# Revit family: PDU medido 0U
name_source: partatom
category: Installations électriques
units: mm (PartAtom-declared; Revit-internal decimal feet)

## family parameters
Basée sur le plan de construction = Non
Conserver l'orientation des annotations = Non
Cote de connecteur circulaire = Utiliser le diamètre
Couper avec des vides une fois chargée = Non
Numéro OmniClass = 23.80.00.00
Partagée = Non
Point de calcul de pièce = Non
Titre OmniClass = Electric Power and Lighting
Toujours verticalement = Oui
Type d'élément = Normal

## types (16) — shared parameters
Clase de aplicación = EC002762
Color = Negro
Conectable con internet box = Oui
Consumo pasivo = 0 mA
Dirección de montaje = Vertical
E-catalogo enlace = https://www.legrand.fr
Fabricant = LEGRAND
Formulación BIM = Linkeo DATA CENTER BASIC PDU
Frecuencia eléctrica = 50-50
Función = Unidad DE DISTRIBUTION D'ENERGIE
IP = IP40
Marcaje = Non
Numero RAL = 9017
Prise_alimentation = Alimentation : Prise rotative
Profondeur cuve + capot = 58 mm
Programación = Appli Web
Tipo de tensión = AC
zero-valued in all types: Elévation par défaut

## per-type parameters (varying)
| type | 646102_646103 | 646104_646105 | 646106_646107 | 646108_646109 | 646110_646111 | 646112_646113 | 646114_646115 | 646116_646117 | Anchura (mm) | Base_Node | Corriente de alimentación | Description | EAN | Longitud | Número de disyuntores | Número de fases | Número de pieza Legrand | Número de tomas C13 | Número de tomas C19 | Position base_node | Profundidad (mm) | Sección de cable MIN_MAX | Tipo de conexión eléctrica |
| PDU MB 0U 1P 16A 18xC13+4xC19 | Oui | Non | Non | Non | Non | Non | Non | Non | 44 mm | Base_Node : Base HD | 16-16 | PDU metered base 0U 1 phase 16A 18+4 C13/C19 locking outlets IEC 60309 | 3414972245814 | 1113 mm  [stored 3.65157 ft] | 0 | 1 | LG-646102 | 18 | 4 | 591 mm  [stored 1.93898 ft] | 66 mm | 2.5-2.5 | CEE 16 A |
| PDU MN 0U 1P 16A 18xC13+4xC19 | Oui | Non | Non | Non | Non | Non | Non | Non | 44 mm | Base_Node : Node HD | 16-16 | PDU metered node 0U 1 phase 16A 18+4 C13/C19 locking outlets IEC 60309 | 3414972245876 | 1113 mm  [stored 3.65157 ft] | 0 | 1 | LG-646103 | 18 | 4 | 591 mm  [stored 1.93898 ft] | 84 mm | 2.5-2.5 | CEE 16 A |
| PDU MB 0U 1P 32A 20xC13+4xC19 | Non | Oui | Non | Non | Non | Non | Non | Non | 44 mm | Base_Node : Base HD | 32-32 | PDU metered base 0U 1 phase 32A 20+4 C13/C19 locking outlets IEC 60309 | 3414972245838 | 1317 mm  [stored 4.32087 ft] | 2 | 1 | LG-646104 | 20 | 4 | 748 mm | 66 mm | 6-6 | CEE 32 A |
| PDU MN 0U 1P 32A 20xC13+4xC19 | Non | Oui | Non | Non | Non | Non | Non | Non | 44 mm | Base_Node : Node HD | 32-32 | PDU metered node 0U 1 phase 32A 20+4 C13/C19 locking outlets IEC 60309 | 3414972245890 | 1317 mm  [stored 4.32087 ft] | 2 | 1 | LG-646105 | 20 | 4 | 748 mm | 84 mm | 6-6 | CEE 32 A |
| PDU MB 0U 1P 32A 24xC13+12xC19 | Non | Non | Oui | Non | Non | Non | Non | Non | 52 mm  [stored 0.170604 ft] | Base_Node : Base HD | 32-32 | PDU HD metered base 0U 1 phase 32A 24+12 C13/C19 locking outlets IEC 60309 | 3414972245579 | 1458 mm  [stored 4.78346 ft] | 2 | 1 | LG-646106 | 24 | 12 | 817 mm | 73 mm | 6-6 | CEE 32 A |
| PDU MN 0U 1P 32A 24xC13+12xC19 | Non | Non | Oui | Non | Non | Non | Non | Non | 52 mm  [stored 0.170604 ft] | Base_Node : Node HD | 32-32 | PDU HD metered node 0U 1 phase 32A 24+12 C13/C19 locking outlets IEC 60309 | 3414972245692 | 1458 mm  [stored 4.78346 ft] | 2 | 1 | LG-646107 | 24 | 12 | 817 mm | 91 mm | 6-6 | CEE 32 A |
| PDU MB 0U 1P 32A 36xC13+6xC19 | Non | Non | Non | Oui | Non | Non | Non | Non | 52 mm  [stored 0.170604 ft] | Base_Node : Base HD | 32-32 | PDU HD metered base 0U 1 phase 32A 36+6 C13/C19 locking outlets IEC 60309 | 3414972245593 | 1440 mm  [stored 4.72441 ft] | 2 | 1 | LG-646108 | 36 | 6 | 808 mm | 73 mm | 6-6 | CEE 32 A |
| PDU MN 0U 1P 32A 36xC13+6xC19 | Non | Non | Non | Oui | Non | Non | Non | Non | 52 mm  [stored 0.170604 ft] | Base_Node : Node HD | 32-32 | PDU HD metered node 0U 1 phase 32A 36+6 C13/C19 locking outlets IEC 60309 | 3414972245715 | 1440 mm  [stored 4.72441 ft] | 2 | 1 | LG-646109 | 36 | 6 | 808 mm | 91 mm | 6-6 | CEE 32 A |
| PDU MB 0U 3P 16A 36xC13+6xC19 | Non | Non | Non | Non | Oui | Non | Non | Non | 52 mm  [stored 0.170604 ft] | Base_Node : Base HD | 16-16 | PDU HD metered base 0U 3 phase 16A 36+6 C13/C19 locking outlets IEC 60309 | 3414972245616 | 1350 mm  [stored 4.42913 ft] | 0 | 3 | LG-646110 | 36 | 6 | 877 mm | 73 mm | 2.5-2.5 | CEE 16 A |
| PDU MN 0U 3P 16A 36xC13+6xC19 | Non | Non | Non | Non | Oui | Non | Non | Non | 52 mm  [stored 0.170604 ft] | Base_Node : Node HD | 16-16 | PDU HD metered node 0U 3 phase 16A 36+6 C13/C19 locking outlets IEC 60309 | 3414972245739 | 1350 mm  [stored 4.42913 ft] | 0 | 3 | LG-646111 | 36 | 6 | 877 mm | 91 mm | 2.5-2.5 | CEE 16 A |
| PDU MB 0U 3P 32A 24xC13+12xC19 | Non | Non | Non | Non | Non | Oui | Non | Non | 52 mm  [stored 0.170604 ft] | Base_Node : Base HD | 32-32 | PDU HD metered base 0U 3 phase 32A 24+12 C13/C19 locking outlets IEC 60309 | 3414972245630 | 1728 mm  [stored 5.66929 ft] | 6 | 3 | LG-646112 | 24 | 12 | 952 mm  [stored 3.12336 ft] | 73 mm | 6-6 | CEE 32 A |
| PDU MN 0U 3P 32A 24xC13+12xC19 | Non | Non | Non | Non | Non | Oui | Non | Non | 52 mm  [stored 0.170604 ft] | Base_Node : Node HD | 32-32 | PDU HD metered node 0U 3 phase 32A 24+12 C13/C19 locking outlets IEC 60309 | 3414972245753 | 1728 mm  [stored 5.66929 ft] | 6 | 3 | LG-646113 | 24 | 12 | 952 mm  [stored 3.12336 ft] | 91 mm | 6-6 | CEE 32 A |
| PDU MB 0U 3P 32A 36xC13+12xC19 | Non | Non | Non | Non | Non | Non | Oui | Non | 52 mm  [stored 0.170604 ft] | Base_Node : Base HD | 32-32 | PDU HD metered base 0U 3 phase 32A 36+12 C13/C19 locking out. IEC 60309 | 3414972245654 | 1962 mm  [stored 6.43701 ft] | 6 | 3 | LG-646114 | 36 | 12 | 1068 mm | 73 mm | 6-6 | CEE 32 A |
| PDU MN 0U 3P 32A 36xC13+12xC19 | Non | Non | Non | Non | Non | Non | Oui | Non | 52 mm  [stored 0.170604 ft] | Base_Node : Node HD | 32-32 | PDU HD metered node 0U 3 phase 32A 36+12 C13/C19 locking out. IEC 60309 | 3414972245777 | 1962 mm  [stored 6.43701 ft] | 6 | 3 | LG-646115 | 36 | 12 | 1068 mm | 91 mm | 6-6 | CEE 32 A |
| PDU MB 0U 3P 32A 36xC13+6xC19 | Non | Non | Non | Non | Non | Non | Non | Oui | 52 mm  [stored 0.170604 ft] | Base_Node : Base HD | 32-32 | PDU HD metered base 0U 3 phase 32A 36+6 C13/C19 locking outlets IEC 60309 | 3414972245678 | 1710 mm  [stored 5.61024 ft] | 6 | 3 | LG-646116 | 36 | 6 | 942 mm | 73 mm | 6-6 | CEE 32 A |
| PDU MN 0U 3P 32A 36xC13+6xC19 | Non | Non | Non | Non | Non | Non | Non | Oui | 52 mm  [stored 0.170604 ft] | Base_Node : Node HD | 32-32 | PDU HD metered node 0U 3 phase 32A 36+6 C13/C19 locking outlets IEC 60309 | 3414972245791 | 1710 mm  [stored 5.61024 ft] | 6 | 3 | LG-646117 | 36 | 6 | 942 mm | 91 mm | 6-6 | CEE 32 A |

note: [stored X ft] marks values corroborated as IEEE doubles in the binary element streams (Revit-internal decimal feet)
